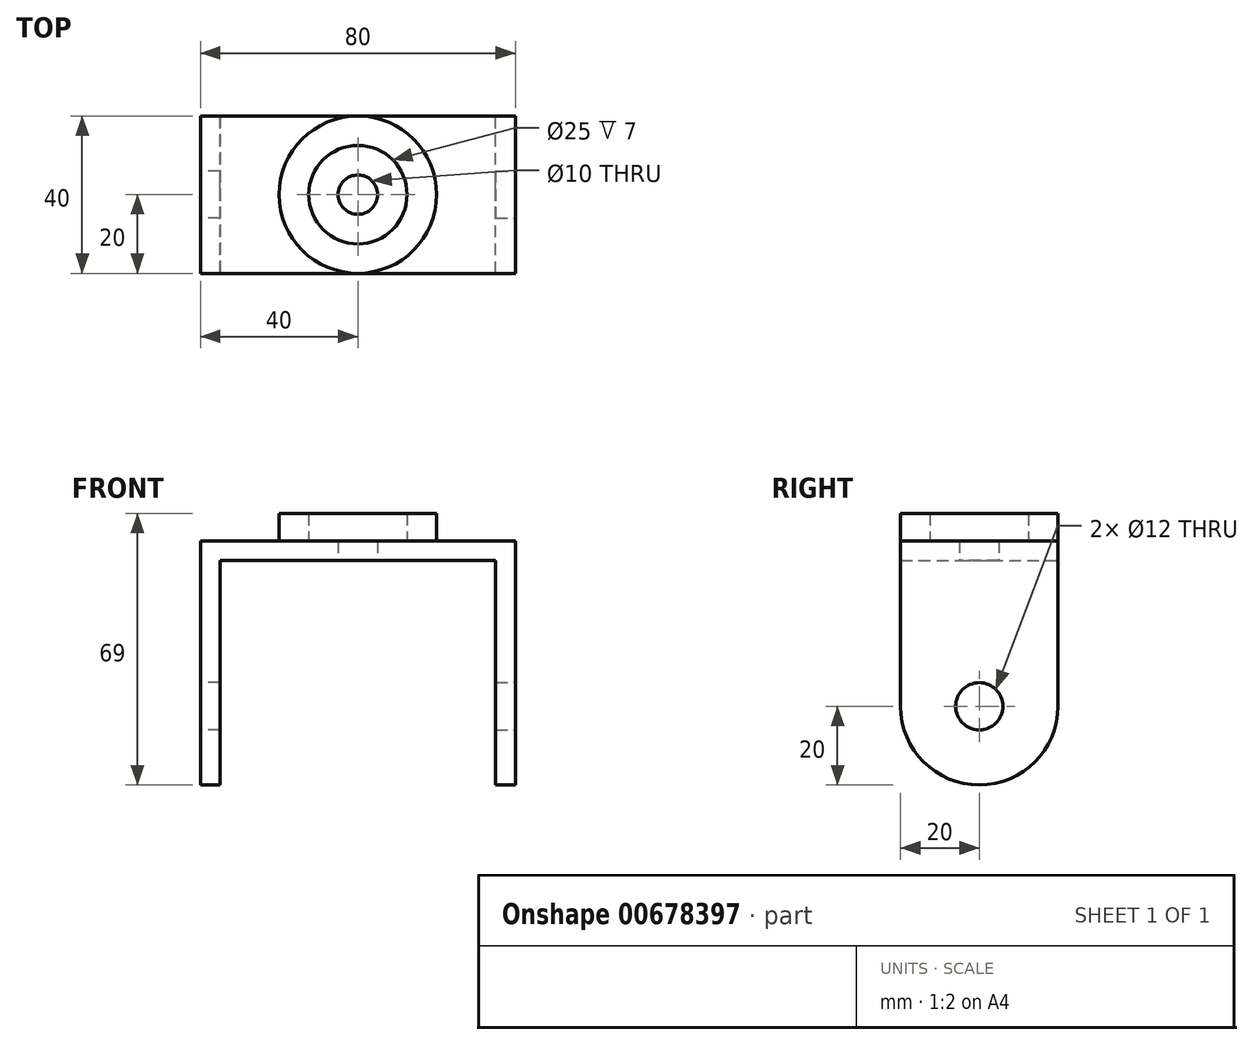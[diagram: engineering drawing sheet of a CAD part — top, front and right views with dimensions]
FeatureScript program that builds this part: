
annotation { "Feature Type Name" : "Feature", "Feature Type Description" : "" }
export const myFeature = defineFeature(function(context is Context, id is Id, definition is map)
    precondition{}
    {
        {
            var Q0;
            Q0=qCreatedBy(makeId("Top.planeOp"),FACE);
            var sketch = newSketch(context, id + "F0", { "sketchPlane" : qUnion([Q0])});
            skLineSegment(sketch, "E0.bottom", {"start": v(40, -20) * mm, "end": v(-40, -20) * mm});
            skLineSegment(sketch, "E0.top", {"start": v(40, 20) * mm, "end": v(-40, 20) * mm});
            skLineSegment(sketch, "E0.left", {"start": v(40, -20) * mm, "end": v(40, 20) * mm});
            skLineSegment(sketch, "E0.right", {"start": v(-40, -20) * mm, "end": v(-40, 20) * mm});
            skPoint(sketch, "E0.middle", {"position": v(0, 0) * mm});
            skCircle(sketch, "E1", {"center": v(0, 0) * mm, "radius": 20 * mm});
            skCircle(sketch, "E2", {"center": v(0, 0) * mm, "radius": 12.5 * mm});
            skLineSegment(sketch, "E3", {"start": v(-40, 20) * mm, "end": v(-35, 20) * mm});
            skLineSegment(sketch, "E4", {"start": v(-35, 20) * mm, "end": v(-35, -20) * mm});
            skLineSegment(sketch, "E5", {"start": v(40, 20) * mm, "end": v(35, 20) * mm});
            skLineSegment(sketch, "E6", {"start": v(35, 20) * mm, "end": v(35, -20) * mm});
            skCircle(sketch, "E7", {"center": v(0, 0) * mm, "radius": 5 * mm});
            skSolve(sketch);
        }
        {
            var Q0;
            Q0 = qSketchRegion(id + "F0", true);
            extrude(context, id + "F1", {"entities" : qUnion([Q0]), "depth" : 5 * mm, "offsetDistance" : 25 * mm});
        }
        {
            var Q0;
            Q0=makeQuery(id+"F0.imprint","IMPRINT",FACE,{"disambiguationData":[TD([[makeQuery(id+"F0.imprint","IMPRINT",EDGE,{"derivedFrom":sQuery(id+"F0.wireOp",EDGE,"E2")}),-1.0]])]});
            extrude(context, id + "F2", {"entities" : qUnion([Q0]), "operationType" : NewBodyOperationType.ADD, "depth" : 12 * mm, "offsetDistance" : 25 * mm});
        }
        {
            var Q0;
            Q0=makeQuery(id+"F0.imprint","IMPRINT",FACE,{"disambiguationData":[TD([[makeQuery(id+"F0.imprint","IMPRINT",EDGE,{"derivedFrom":sQuery(id+"F0.wireOp",EDGE,"E2")}),1.0]])]});
            extrude(context, id + "F3", {"entities" : qUnion([Q0]), "operationType" : NewBodyOperationType.ADD, "depth" : 5 * mm, "offsetDistance" : 25 * mm});
        }
        {
            var Q0;
            Q0=makeQuery(id+"F1.opExtrude","SWEPT_FACE",FACE,{"disambiguationData":[OSD([sQuery(id+"F0.wireOp",EDGE,"E0.left")])]});
            var sketch = newSketch(context, id + "F4", { "sketchPlane" : qUnion([Q0])});
            skLineSegment(sketch, "E8", {"start": v(-20, 0) * mm, "end": v(-20, -37) * mm});
            skLineSegment(sketch, "E9", {"start": v(20, 0) * mm, "end": v(20, -37) * mm});
            skArc(sketch, "E10", {"start": v(-20, -37) * mm, "mid": v(0, -57) * mm, "end": v(20, -37) * mm});
            skCircle(sketch, "E11", {"center": v(0, -37) * mm, "radius": 6 * mm});
            skSolve(sketch);
        }
        {
            var Q0;
            Q0=makeQuery(id+"F4.imprint","IMPRINT",FACE,{"disambiguationData":[TD([[makeQuery(id+"F4.imprint","IMPRINT",EDGE,{"derivedFrom":sQuery(id+"F4.wireOp",EDGE,"E8")}),1.0]])]});
            extrude(context, id + "F5", {"entities" : qUnion([Q0]), "operationType" : NewBodyOperationType.ADD, "oppositeDirection" : true, "depth" : 5 * mm, "offsetDistance" : 25 * mm});
        }
        {
            var Q0;
            Q0=makeQuery(id+"F1.opExtrude","SWEPT_FACE",FACE,{"disambiguationData":[OSD([sQuery(id+"F0.wireOp",EDGE,"E0.right")])]});
            var sketch = newSketch(context, id + "F6", { "sketchPlane" : qUnion([Q0])});
            skLineSegment(sketch, "E12", {"start": v(-20, 0) * mm, "end": v(-20, -37) * mm});
            skLineSegment(sketch, "E13", {"start": v(20, 0) * mm, "end": v(20, -37) * mm});
            skArc(sketch, "E14", {"start": v(-20, -37) * mm, "mid": v(0, -57) * mm, "end": v(20, -37) * mm});
            skCircle(sketch, "E15", {"center": v(0, -37) * mm, "radius": 6 * mm});
            skSolve(sketch);
        }
        {
            var Q0;
            Q0=makeQuery(id+"F6.imprint","IMPRINT",FACE,{"disambiguationData":[TD([[makeQuery(id+"F6.imprint","IMPRINT",EDGE,{"derivedFrom":sQuery(id+"F6.wireOp",EDGE,"E12")}),1.0]])]});
            extrude(context, id + "F7", {"entities" : qUnion([Q0]), "operationType" : NewBodyOperationType.ADD, "oppositeDirection" : true, "depth" : 5 * mm, "offsetDistance" : 25 * mm});
        }
    });
